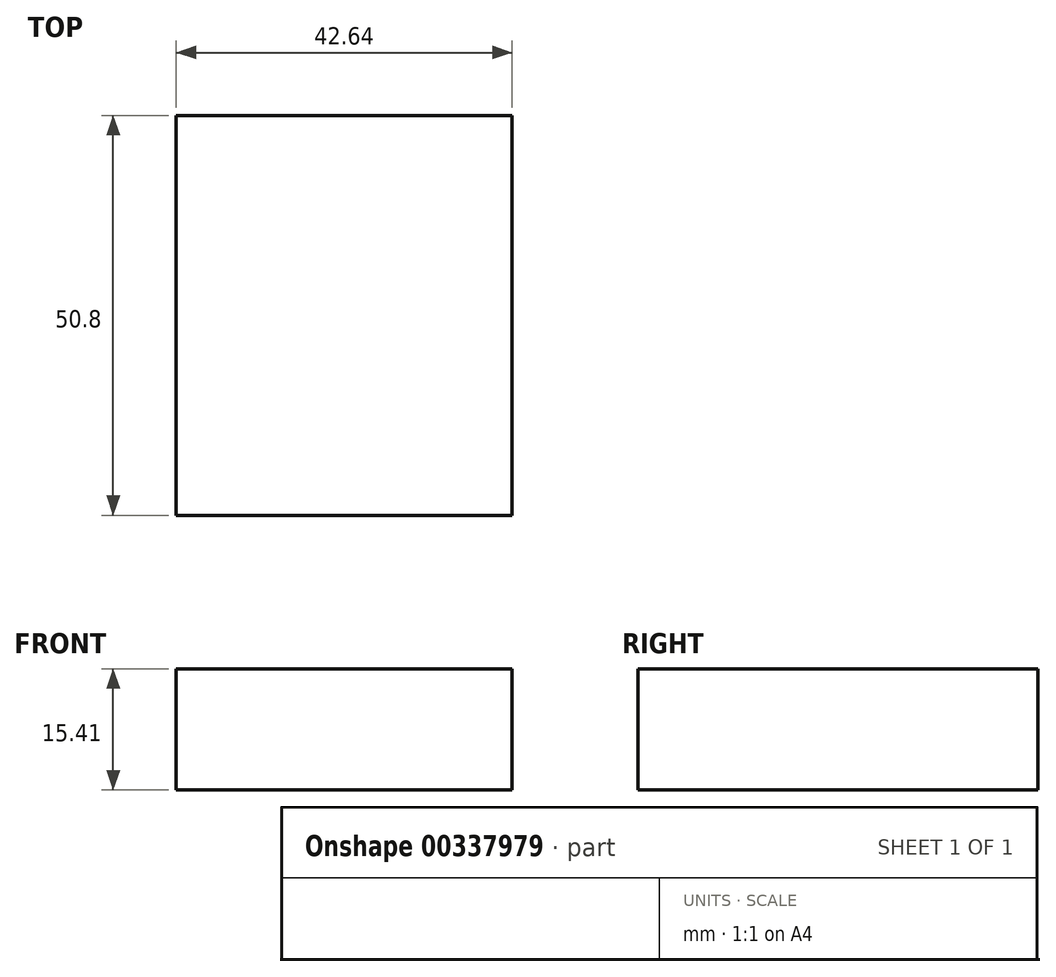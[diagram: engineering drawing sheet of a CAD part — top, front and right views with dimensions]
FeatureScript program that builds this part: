
annotation { "Feature Type Name" : "Feature", "Feature Type Description" : "" }
export const myFeature = defineFeature(function(context is Context, id is Id, definition is map)
    precondition{}
    {
        {
            var Q0;
            Q0=qCreatedBy(makeId("Front.planeOp"),FACE);
            var sketch = newSketch(context, id + "F0", { "sketchPlane" : qUnion([Q0])});
            skLineSegment(sketch, "E0.bottom", {"start": v(-62.9, 58.33) * mm, "end": v(-20.25, 58.33) * mm});
            skLineSegment(sketch, "E0.top", {"start": v(-62.9, 42.92) * mm, "end": v(-20.25, 42.92) * mm});
            skLineSegment(sketch, "E0.left", {"start": v(-62.9, 58.33) * mm, "end": v(-62.9, 42.92) * mm});
            skLineSegment(sketch, "E0.right", {"start": v(-20.25, 58.33) * mm, "end": v(-20.25, 42.92) * mm});
            skSolve(sketch);
        }
        {
            var Q0;
            Q0 = qSketchRegion(id + "F0", true);
            extrude(context, id + "F1", {"entities" : qUnion([Q0]), "depth" : 50.8 * mm});
        }
    });
